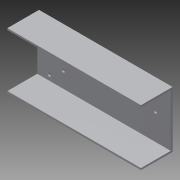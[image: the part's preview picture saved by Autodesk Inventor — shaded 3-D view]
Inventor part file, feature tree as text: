
AUTODESK INVENTOR PART (.ipt)
format: ipt  version: 2013 (Build 170138000, 138)  size: 95,744 bytes
history: native  units: in
note: dims shown in document units (in); Inventor stores cm internally (conversion verified against a paired STEP export)
features: other x4, reference x2, hole x1, sketch x1
ambient origin geometry x8: Origin, YZ Plane, XZ Plane, XY Plane, X Axis, Y Axis, Z Axis, Center Point
bodies: Solid1 (feature_tree)
feature tree (8):
  other  "Table"
  other  "channel2.25x4.ipt"
  hole  "Hole1"  [1 undecoded]
  other  "Solid1::channel2.25x4.ipt"
  other  "TaggingFeature1"
  sketch  "Sketch1"  dims[d0=4.0in d1=2.25in d2=0.125in d4=0.0in d3=0.26in d5=0.75in d6=0.375in d7=0.25in d8=0.5635in d9=1.0in d10=0.8108in]
  reference  "Reference1"
  reference  "Reference2"
note: 1 required parameter value undecoded (feature->parameter linkage not recoverable at this tier; creation-order binding heuristic only, values carry confidence <= 0.55)
